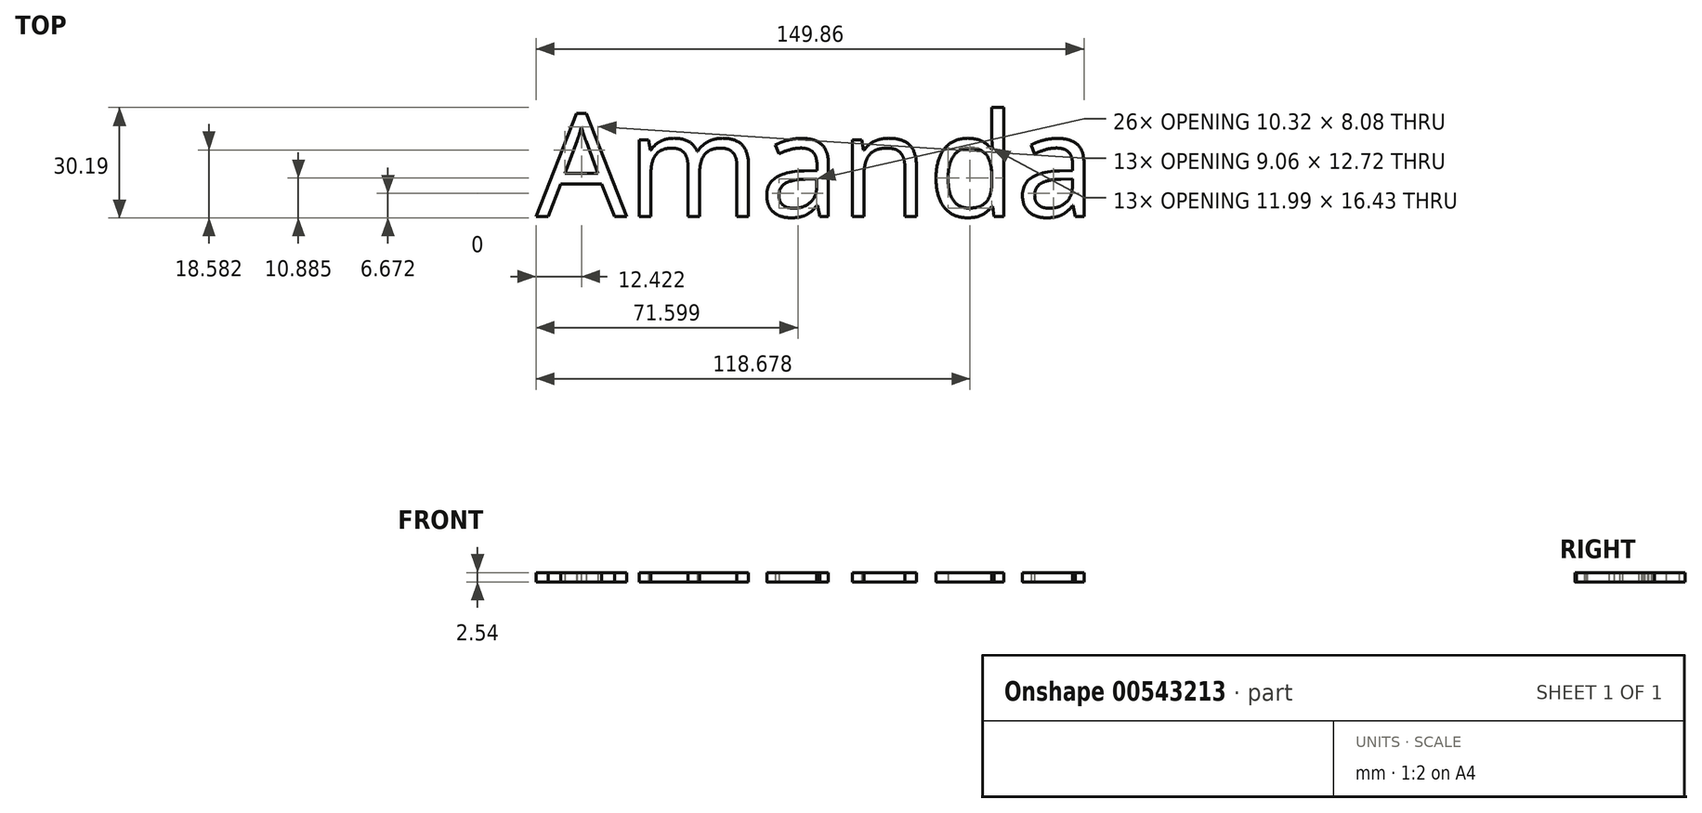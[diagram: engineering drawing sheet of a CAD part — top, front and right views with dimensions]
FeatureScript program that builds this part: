
annotation { "Feature Type Name" : "Feature", "Feature Type Description" : "" }
export const myFeature = defineFeature(function(context is Context, id is Id, definition is map)
    precondition{}
    {
        {
            var Q0;
            Q0=qCreatedBy(makeId("Top.planeOp"),FACE);
            var sketch = newSketch(context, id + "F0", { "sketchPlane" : qUnion([Q0])});
            skText(sketch, "E0", { "text": "Amanda", "fontName": "OpenSans-Regular.ttf"});
            const initialGuessF0  = {"E0": [-0.0744, -0.0089, 1, 0, 0.02824]};
            skSetInitialGuess(sketch, initialGuessF0);
            skSolve(sketch);
        }
        {
            var Q0;
            Q0 = qSketchRegion(id + "F0", true);
            extrude(context, id + "F1", {"entities" : qUnion([Q0]), "depth" : 2.54 * mm, "offsetDistance" : 25.4 * mm});
        }
    });
